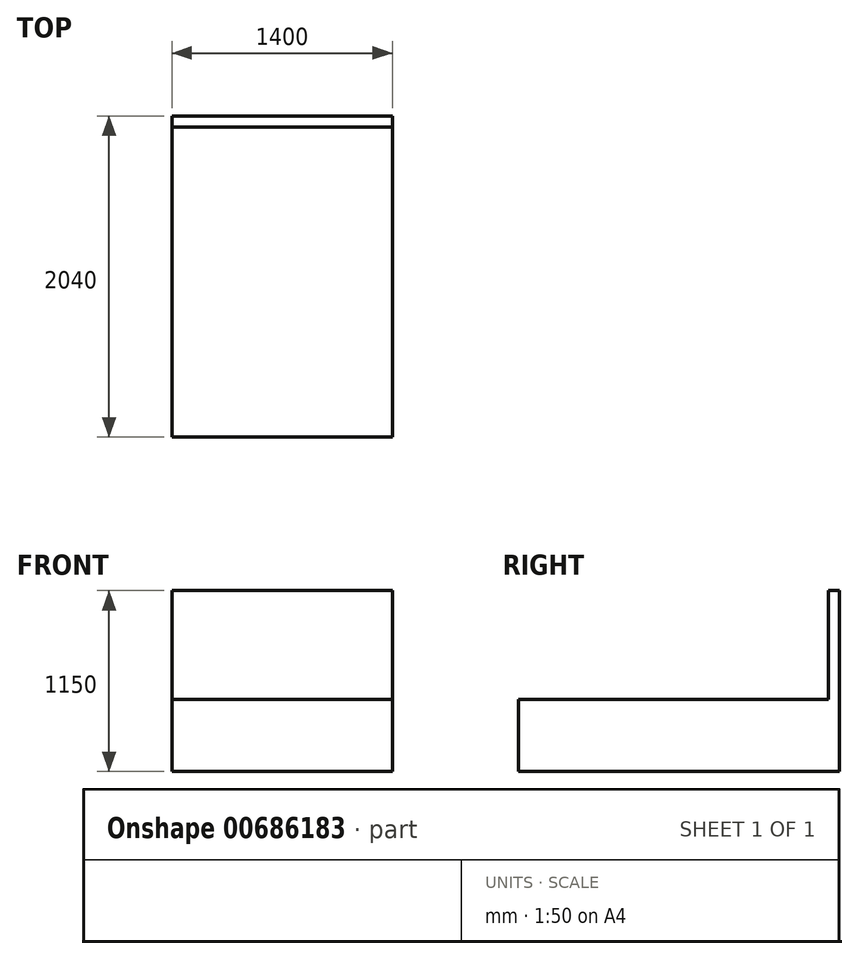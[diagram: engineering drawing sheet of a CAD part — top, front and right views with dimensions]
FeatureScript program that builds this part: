
annotation { "Feature Type Name" : "Feature", "Feature Type Description" : "" }
export const myFeature = defineFeature(function(context is Context, id is Id, definition is map)
    precondition{}
    {
        {
            var Q0;
            Q0=qCreatedBy(makeId("Top.planeOp"),FACE);
            var sketch = newSketch(context, id + "F0", { "sketchPlane" : qUnion([Q0])});
            skLineSegment(sketch, "E0.bottom", {"start": v(0, 0) * mm, "end": v(1400, 0) * mm});
            skLineSegment(sketch, "E0.top", {"start": v(0, 2040) * mm, "end": v(1400, 2040) * mm});
            skLineSegment(sketch, "E0.left", {"start": v(0, 0) * mm, "end": v(0, 2040) * mm});
            skLineSegment(sketch, "E0.right", {"start": v(1400, 0) * mm, "end": v(1400, 2040) * mm});
            skLineSegment(sketch, "E1", {"start": v(0, 1970) * mm, "end": v(1400, 1970) * mm});
            skSolve(sketch);
        }
        {
            var Q0;
            {var subQ0=sQuery(id+"F0.wireOp",EDGE,"E0.bottom");Q0=makeQuery(id+"F0.imprint","IMPRINT",FACE,{"disambiguationData":[TD([[makeQuery(id+"F0.imprint","IMPRINT",EDGE,{"derivedFrom":subQ0}),1.0]])]});}
            extrude(context, id + "F1", {"entities" : qUnion([Q0]), "depth" : 460 * mm, "offsetDistance" : 25 * mm});
        }
        {
            var Q0;
            {var subQ0=sQuery(id+"F0.wireOp",EDGE,"E0.top");Q0=makeQuery(id+"F0.imprint","IMPRINT",FACE,{"disambiguationData":[TD([[makeQuery(id+"F0.imprint","IMPRINT",EDGE,{"derivedFrom":subQ0}),-1.0]])]});}
            extrude(context, id + "F2", {"entities" : qUnion([Q0]), "operationType" : NewBodyOperationType.ADD, "depth" : 1150 * mm, "offsetDistance" : 25 * mm});
        }
    });
